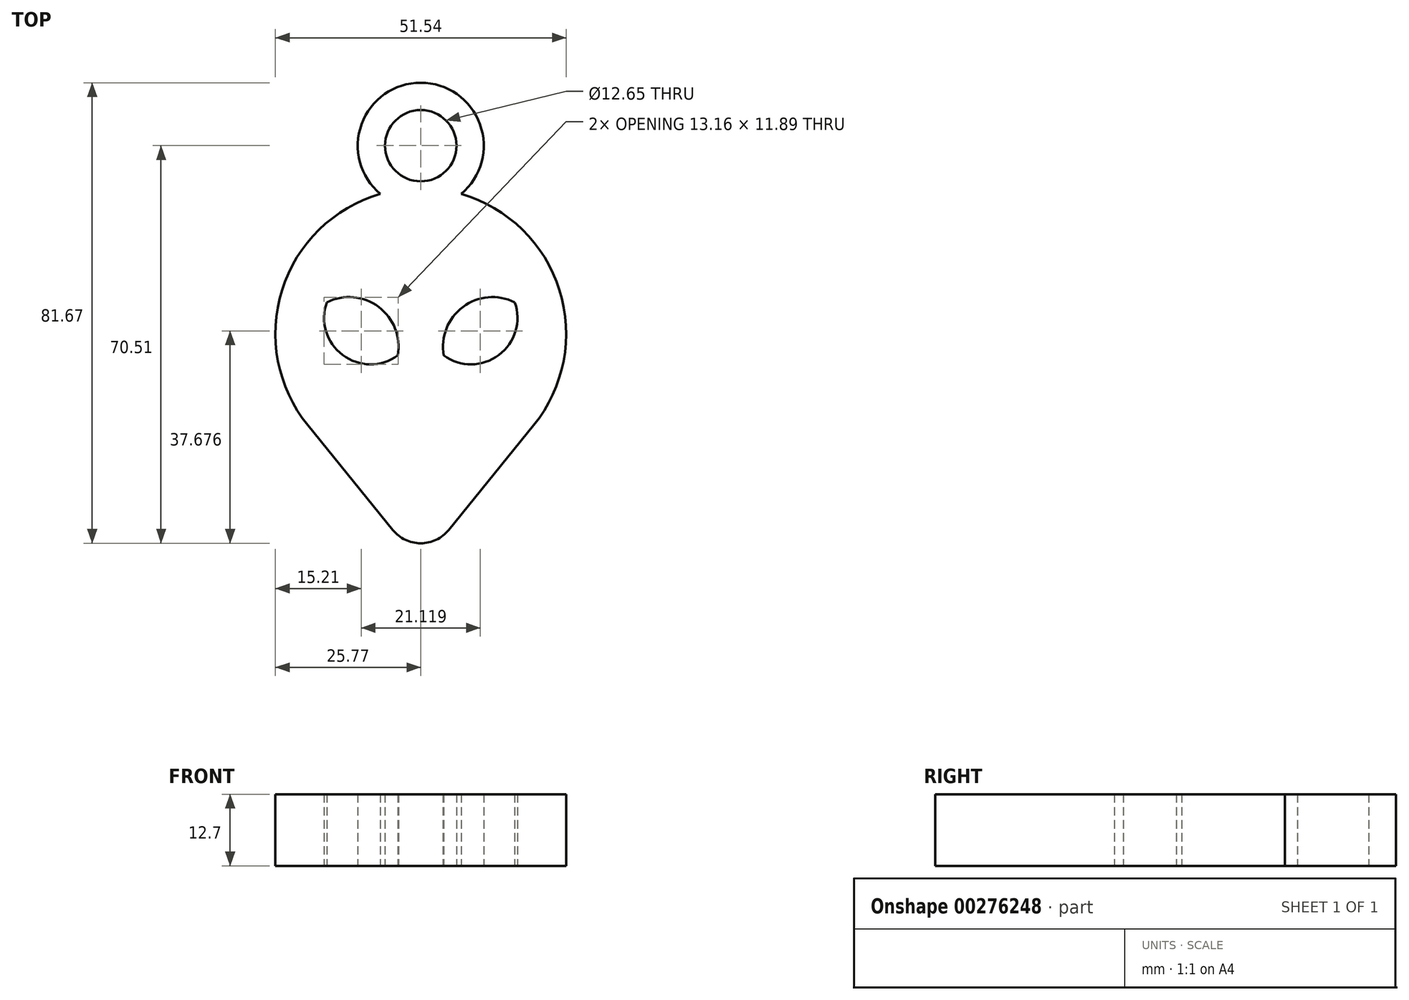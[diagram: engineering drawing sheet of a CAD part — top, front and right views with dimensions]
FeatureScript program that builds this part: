
annotation { "Feature Type Name" : "Feature", "Feature Type Description" : "" }
export const myFeature = defineFeature(function(context is Context, id is Id, definition is map)
    precondition{}
    {
        {
            var Q0;
            Q0=qCreatedBy(makeId("Top.planeOp"),FACE);
            var sketch = newSketch(context, id + "F0", { "sketchPlane" : qUnion([Q0])});
            skArc(sketch, "E0", {"start": v(20.01, -16.24) * mm, "mid": v(0, 25.77) * mm, "end": v(-20.01, -16.24) * mm});
            skLineSegment(sketch, "E1", {"start": v(4.93, -34.83) * mm, "end": v(20.01, -16.24) * mm});
            skLineSegment(sketch, "E2", {"start": v(-4.93, -34.83) * mm, "end": v(-20.01, -16.24) * mm});
            skPoint(sketch, "E3.visualSharp", {"position": v(0, -40.9) * mm});
            skArc(sketch, "E3.filletArc", {"start": v(-4.93, -34.83) * mm, "mid": v(0, -37.18) * mm, "end": v(4.93, -34.83) * mm});
            skArc(sketch, "E4", {"start": v(-4.07, -3.88) * mm, "mid": v(-7.46, 4.72) * mm, "end": v(-16.66, 5.56) * mm});
            skArc(sketch, "E5", {"start": v(-16.66, 5.56) * mm, "mid": v(-13.85, -3.8) * mm, "end": v(-4.07, -3.88) * mm});
            skArc(sketch, "E6.MirrorCS", {"start": v(4.07, -3.88) * mm, "mid": v(7.46, 4.72) * mm, "end": v(16.66, 5.56) * mm});
            skArc(sketch, "E7.MirrorCS", {"start": v(16.66, 5.56) * mm, "mid": v(13.85, -3.8) * mm, "end": v(4.07, -3.88) * mm});
            skPoint(sketch, "E8.start.orphan", {"position": v(0, 9.58) * mm});
            skSolve(sketch);
        }
        {
            var Q0;
            Q0=makeQuery(id+"F0.imprint","IMPRINT",FACE,{"disambiguationData":[TD([[makeQuery(id+"F0.imprint","IMPRINT",EDGE,{"derivedFrom":sQuery(id+"F0.wireOp",EDGE,"E0")}),1.0]])]});
            extrude(context, id + "F1", {"entities" : qUnion([Q0]), "depth" : 12.7 * mm});
        }
        {
            var Q0;
            Q0=makeQuery(id+"F1.opExtrude","CAP_FACE",FACE,{"disambiguationData":[OSD([sQuery(id+"F0.wireOp",EDGE,"E0"),sQuery(id+"F0.wireOp",EDGE,"E1"),sQuery(id+"F0.wireOp",EDGE,"E2"),sQuery(id+"F0.wireOp",EDGE,"E3.filletArc"),sQuery(id+"F0.wireOp",EDGE,"E4"),sQuery(id+"F0.wireOp",EDGE,"E5"),sQuery(id+"F0.wireOp",EDGE,"E6.MirrorCS"),sQuery(id+"F0.wireOp",EDGE,"E7.MirrorCS")])],"isStart":true});
            var sketch = newSketch(context, id + "F2", { "sketchPlane" : qUnion([Q0])});
            skArc(sketch, "E9", {"start": v(-7.16, -24.76) * mm, "mid": v(0, -44.5) * mm, "end": v(7.16, -24.76) * mm});
            skCircle(sketch, "E10", {"center": v(0, -33.33) * mm, "radius": 6.33 * mm});
            skPoint(sketch, "E11", {"position": v(-7.16, -24.76) * mm});
            skPoint(sketch, "E12", {"position": v(7.16, -24.76) * mm});
            skSolve(sketch);
        }
        {
            var Q0;
            {var subQ0=sQuery(id+"F2.wireOp",EDGE,"E9");Q0=makeQuery(id+"F2.imprint","IMPRINT",FACE,{"disambiguationData":[TD([[makeQuery(id+"F2.imprint","IMPRINT",EDGE,{"derivedFrom":subQ0}),1.0]])]});}
            extrude(context, id + "F3", {"entities" : qUnion([Q0]), "operationType" : NewBodyOperationType.ADD, "oppositeDirection" : true, "depth" : 12.7 * mm});
        }
    });
